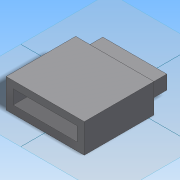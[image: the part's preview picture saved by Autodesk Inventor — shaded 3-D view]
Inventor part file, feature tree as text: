
AUTODESK INVENTOR PART (.ipt)
format: ipt  version: 2014 SP2 (Build 180246200, 246)  size: 120,320 bytes
history: native  units: in
note: dims shown in document units (in); Inventor stores cm internally (conversion verified against a paired STEP export)
features: other x3, plane x1, extrude x1, sketch x1, projected_geometry x1
ambient origin geometry x8: Origin, YZ Plane, XZ Plane, XY Plane, X Axis, Y Axis, Z Axis, Center Point
bodies: Solid1 (feature_tree)
feature tree (7):
  other  "jst-xh 7c.ipt"
  plane  "Work Plane1"
  extrude  "Extrusion1"  [1 undecoded]
  other  "Solid1::jst-xh 7c.ipt"
  other  "TaggingFeature1"
  sketch  "Sketch1"  dims[d0=0.3937in d1=-0.225in d2=0.08in d3=0.09in d4=0.08in d5=0.08in d6=0.783in d7=0.0in]
  projected_geometry  "Projected Loop1"
note: 1 required parameter value undecoded (feature->parameter linkage not recoverable at this tier; creation-order binding heuristic only, values carry confidence <= 0.55)
